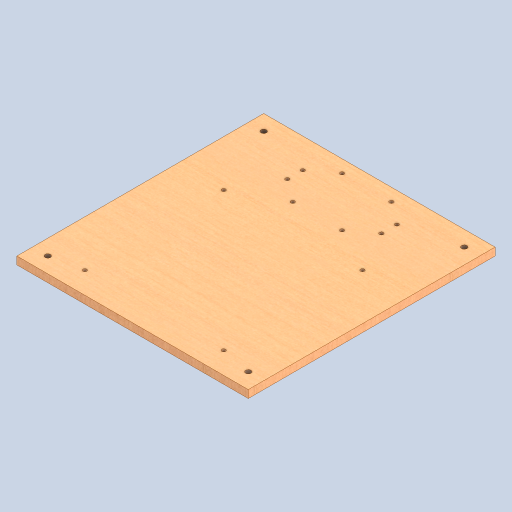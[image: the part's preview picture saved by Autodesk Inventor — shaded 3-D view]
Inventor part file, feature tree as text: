
AUTODESK INVENTOR PART (.ipt)
format: ipt  version: 2023 (Build 270158000, 158)  size: 361,984 bytes
history: native  units: mm
features: sketch x3, hole x2, other x1, extrude x1
ambient origin geometry x8: Origin, YZ Plane, XZ Plane, XY Plane, X Axis, Y Axis, Z Axis, Center Point
bodies: Body1 (feature_tree)
feature tree (7):
  other  "Sólido1"
  extrude  "Extrusão1"  Depth=320.0mm
  hole  "Hole1"  [1 undecoded]
  hole  "Hole2"  [1 undecoded]
  sketch  "Esboço1"  dims[d0=300.0mm d1=320.0mm]
  sketch  "Sketch2"  dims[d2=10.0mm d3=0.0mm]
  sketch  "Sketch3"  dims[d5=20.0mm d7=20.0mm d9=20.0mm d11=20.0mm d13=20.0mm d15=20.0mm d16=64.0mm d17=64.0mm d18=300.0mm d19=320.0mm d20=16.4mm d21=118.0mm d22=122.0mm d23=20.0mm d24=38.4mm d25=89.0mm d26=180.0mm d27=180.0mm d28=60.0mm d29=28.1mm d30=5.0mm d31=6.0mm d32=4.0mm d33=2.0mm d34=90.0deg d35=0.5mm d36=20.594885mm d38=20.0mm d40=20.0mm d41=280.0mm d42=260.0mm d43=320.0mm d44=300.0mm d45=20.0mm d46=20.0mm d47=7.133974mm d48=16.0mm d49=4.0mm d50=2.0mm d51=90.0deg d52=8.0mm d53=20.594885mm]
note: 2 required parameter values undecoded (feature->parameter linkage not recoverable at this tier; creation-order binding heuristic only, values carry confidence <= 0.55)
